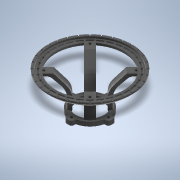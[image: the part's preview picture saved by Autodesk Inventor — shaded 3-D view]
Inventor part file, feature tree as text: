
AUTODESK INVENTOR PART (.ipt)
format: ipt  version: 2020 (Build 240168000, 168)  size: 1,798,656 bytes
history: native  units: mm
features: projected_geometry x28, other x27, sketch x23, extrude x13, fillet x10, revolve x9, pattern_circular x6, loft x6, mirror x5, chamfer x2
ambient origin geometry x8: Origin, YZ Plane, XZ Plane, XY Plane, X Axis, Y Axis, Z Axis, Center Point
bodies: Body1 (feature_tree)
feature tree (129):
  other  "Твердое тело1"
  extrude  "Выдавливание1"  Depth=34.0mm
  other  "РабПлоскость1"
  other  "РабОсь1"
  revolve  "Вращение1"
  extrude  "Выдавливание2"  Depth=45.0mm
  other  "РабТочка2"
  other  "РабТочка3"
  other  "РабТочка4"
  other  "РабПлоскость2"
  sketch  "Эскиз5"
  revolve  "Вращение2"
  revolve  "Вращение3"
  pattern_circular  "Круговой массив1"  Angle=45.0deg  [1 undecoded]
  extrude  "Выдавливание3"  Depth=2.9mm
  revolve  "Вращение4"
  fillet  "Сопряжение1"  Radius=9.0mm
  revolve  "Вращение5"
  other  "РабПлоскость6"
  other  "РабПлоскость7"
  sketch  "Эскиз10"
  revolve  "Вращение6"
  revolve  "Вращение7"
  sketch  "Эскиз11"
  sketch  "Эскиз12"
  loft  "Лофт2"
  loft  "Лофт3"
  fillet  "Сопряжение2"  Radius=1.0mm
  extrude  "Выдавливание4"  Depth=22.0mm
  loft  "Лофт4"
  fillet  "Сопряжение3"  Radius=5.0mm
  pattern_circular  "Круговой массив2"  [2 undecoded]
  revolve  "Вращение8"
  revolve  "Вращение9"
  extrude  "Выдавливание5"  Depth=2.5mm
  extrude  "Выдавливание6"  Depth=45.0mm
  pattern_circular  "Круговой массив3"  [2 undecoded]
  other  "РабПлоскость8"
  extrude  "Выдавливание8"  Depth=2.0mm
  extrude  "Выдавливание7"  Depth=2.0mm
  loft  "Лофт5"
  pattern_circular  "Круговой массив4"  Angle=45.0deg  [1 undecoded]
  fillet  "Сопряжение4"  [1 undecoded]
  chamfer  "Фаска1"  Distance=3.0mm
  sketch  "Эскиз23"
  extrude  "Выдавливание9"  TaperAngle=135.0deg  [1 undecoded]
  loft  "Лофт6"
  other  "РабПлоскость9"
  mirror  "Зеркальное отражение1"
  pattern_circular  "Круговой массив5"  [2 undecoded]
  extrude  "Выдавливание10"  TaperAngle=0.0deg  [1 undecoded]
  pattern_circular  "Круговой массив6"  [2 undecoded]
  other  "board plane"
  sketch  "Эскиз26"
  extrude  "Выдавливание11"  Depth=10.0mm
  extrude  "Выдавливание12"  Depth=2.0mm
  other  "РабПлоскость11"
  sketch  "Эскиз28"
  other  "РабПлоскость12"
  loft  "Лофт9"
  fillet  "Сопряжение5"  [1 undecoded]
  other  "РабПлоскость13"
  extrude  "Выдавливание13"  Depth=2.5mm
  chamfer  "Фаска2"  Angle=90.0deg  [1 undecoded]
  other  "РабПлоскость14"
  mirror  "Зеркальное отражение4"
  mirror  "Зеркальное отражение5"
  fillet  "Сопряжение6"  [1 undecoded]
  other  "РабПлоскость15"
  mirror  "Зеркальное отражение6"
  mirror  "Зеркальное отражение7"
  fillet  "Сопряжение8"  Radius=40.0mm
  fillet  "Сопряжение9"  Radius=78.0mm
  fillet  "Сопряжение10"  [1 undecoded]
  fillet  "Сопряжение11"  Radius=2.9mm
  sketch  "Эскиз1"
  sketch  "Эскиз2"
  sketch  "Эскиз4"
  projected_geometry  "Спроецированная петля1"
  projected_geometry  "Спроецированная петля2"
  projected_geometry  "Спроецированная петля3"
  other  "РабПлоскость3"
  other  "РабПлоскость4"
  other  "РабПлоскость5"
  sketch  "Эскиз6"
  sketch  "Эскиз7"
  sketch  "Эскиз9"
  projected_geometry  "Спроецированная петля4"
  projected_geometry  "Спроецированная петля5"
  other  "Ребра2"
  other  "Ребра3"
  sketch  "Эскиз13"
  projected_geometry  "Спроецированная петля6"
  projected_geometry  "Спроецированная петля7"
  sketch  "Эскиз14"
  projected_geometry  "Спроецированная петля8"
  projected_geometry  "Спроецированная петля9"
  projected_geometry  "Спроецированная петля10"
  sketch  "Эскиз16"
  sketch  "Эскиз17"
  projected_geometry  "Спроецированная петля12"
  projected_geometry  "Спроецированная петля13"
  sketch  "Эскиз18"
  sketch  "Эскиз19"
  projected_geometry  "Спроецированная петля14"
  projected_geometry  "Спроецированная петля15"
  other  "Ребра5"
  sketch  "Эскиз22"
  projected_geometry  "Спроецированная петля16"
  projected_geometry  "Спроецированная петля17"
  projected_geometry  "Спроецированная петля18"
  projected_geometry  "Спроецированная петля19"
  projected_geometry  "Спроецированная петля20"
  sketch  "Эскиз24"
  other  "Ребра6"
  sketch  "Эскиз25"
  projected_geometry  "Спроецированная петля21"
  projected_geometry  "Спроецированная петля22"
  projected_geometry  "Спроецированная петля23"
  projected_geometry  "Спроецированная петля24"
  projected_geometry  "Спроецированная петля27"
  projected_geometry  "Спроецированная петля28"
  projected_geometry  "Спроецированная петля29"
  projected_geometry  "Спроецированная петля30"
  sketch  "Эскиз29"
  other  "Ребра15"
  projected_geometry  "Спроецированная петля31"
  other  "Ребра16"
  other  "Ребра17"
note: 17 required parameter values undecoded (feature->parameter linkage not recoverable at this tier; creation-order binding heuristic only, values carry confidence <= 0.55)
